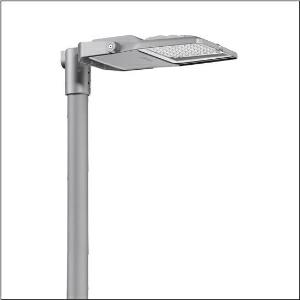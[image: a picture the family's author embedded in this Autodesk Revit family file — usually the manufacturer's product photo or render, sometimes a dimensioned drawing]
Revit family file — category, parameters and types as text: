
# Revit family: floodlight_fl_21_iq_mini___pl43_5xa7772c4a3a_a38e
name_source: partatom
category: Lighting Fixtures
units: mm (PartAtom-declared; Revit-internal decimal feet)

## family parameters
Cut with Voids When Loaded = No
Host = Face
Light Source = No
Part Type = Normal
Room Calculation Point = No
Round Connector Dimension = Use Diameter
Shared = No

## types (1)
- --- (1 x LED, 13050 lm, 87.2 W, 4000K)
    Apparent Load = 87 VA
    CIE Flux Codes = 27 78 99 100 100
    Color Rendering = 70
    Color Temperature = 4000K
    Default Elevation = 1800 mm
    Description = Floodlight FL 21 iQ mini, floodlight, primary light control with lens, of PMMA, primary optical cover: protective disc, of toughened safety glass, transparent, light distribution: PL43, light emission: direct distribution, installation type: surface-mounted, lamps: LED, High Power LED, rated values: 13.050lm | 87,2W | 149,7lm/W (begin service life); end service life: 13.050lm | 92,1W; at 50% lumin. flux: 6.525lm | 40,2W | 162,3lm/W, colour temperature: 4000K, colour rendering: CRI > 70, light colour: 740, light setting 1 begin service life: 100% | 13.050lm | 87,2W | 149,7lm/W | 4.000K, light setting 1 end service life: 92,1W, further light settings possible, control: pre-setting: linear dimming characteristic, Auto-Match, Temp-Guard, Night-Set, Smart-Wire, Desk-Remote (wireless, voltage-free reading and setting of iQ features in the workshop via application-optimized NFC function/RFID function), optimised constant luminous flux control (CLO 2.0), Light-Fading, Lumen-Switch, with terminal, 6-pole, mains connection: 220..240V, AC, 50/60Hz, luminaire housing, of diecast aluminium, powder-coated, SITECO metallic grey (DB 702S), corrosivity category C5 mid according to DIN EN ISO 12944suitable for swimming poolschlorine-resistant, sealing non-destructively replaceable, please order mast flange separately, mast bracket, of steel, galvanised, powder-coated, protection rating (complete): IP66, insulation class (complete): insulation class II (safety insulation), certification: CE, ENEC, VDE, protection symbol: D, impact resistance: IK08, permissible operating ambient temperature: -40..+40°C, permissible operating ambient temperature for outdoor applications: -40..+50°C, standard: DIN EN 12944, LABS conformity tested according to VDMA 24364:2018-05, packaging unit: 1 piece

Light Distribution: PL43
    Height = 70 mm
    Lamp = 1 x LED
    Lamp Light Flux = 13050 lm
    Lamp Power = 87.2 W
    Lamp count = 1
    Length = 485 mm
    Luminous efficacy = 150 lm/W
    Manufacturer = Siteco
    ModVariant = No
    Model = 5XA7772C4A3A
    Mounting Place = Pole
    Mounting Type = Pole annexe
    Number of Poles = 1
    OnlyDefault = Yes
    Power Factor = 1
    Product Name = Floodlight FL 21 iQ mini | PL43
    Product group = floodlight | pylon annexe
    ProductGroupID = 6201
    Protection Class = Protection class II
    Protection Degree = IP 66
    RLX_Detail_Level = 1
    RLX_Emergency_Light_Flux = 0 lm
    RLX_Emergency_Type = 0
    RLX_Emergency_Type_DB = No
    RlxData = <blob elided: 101501 chars, md5=a39d9b0a>
    Socket = socket
    Standby Power = 0 W
    System Light Flux = 13050 lm
    System Power = 87 W
    Type Comments = factory setting: luminous flux: 100 % | dim-lin: 254 | 456 mA
    Type Image = l_1007125.jpg
    URL = http://relux.com
    VarID = @adj_163179
    Voltage = 0 V
    Weight = 0.00 kg
    Width = 337 mm

## geometry (parser evidence)
native form markers: Blend x4, Sweep x12
no freeform markers — native parametric forms only
